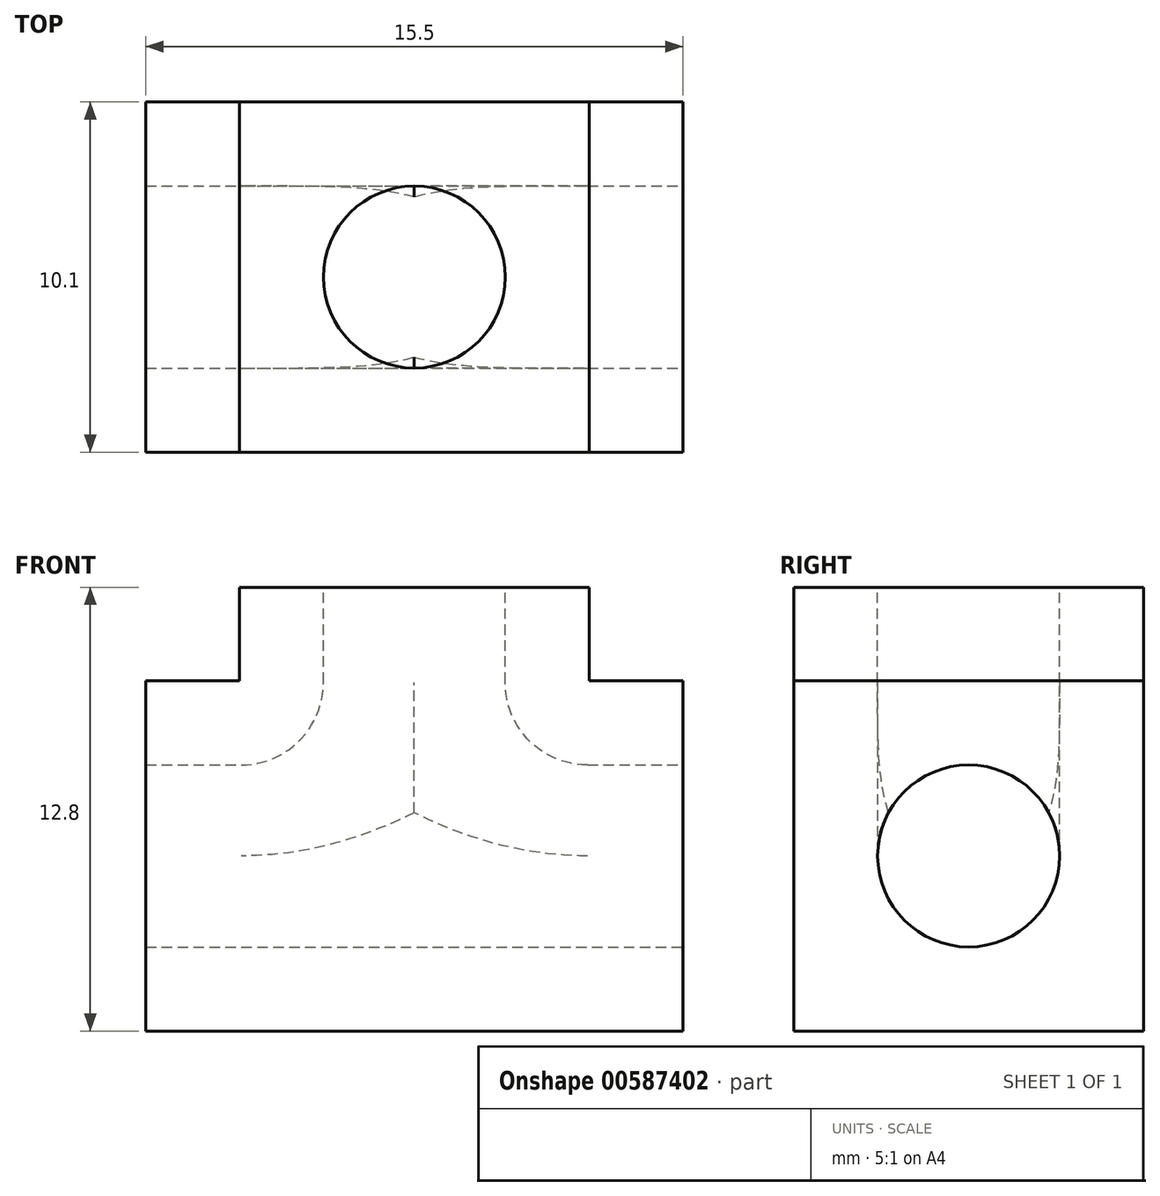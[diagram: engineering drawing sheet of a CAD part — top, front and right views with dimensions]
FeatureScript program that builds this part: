
annotation { "Feature Type Name" : "Feature", "Feature Type Description" : "" }
export const myFeature = defineFeature(function(context is Context, id is Id, definition is map)
    precondition{}
    {
        {
            var Q0;
            Q0=qCreatedBy(makeId("Front.planeOp"),FACE);
            var sketch = newSketch(context, id + "F0", { "sketchPlane" : qUnion([Q0])});
            skLineSegment(sketch, "E0", {"start": v(-15.52, 0) * mm, "end": v(18.58, 0) * mm, "construction": true});
            skLineSegment(sketch, "E1", {"start": v(0, 9.32) * mm, "end": v(0, -7.34) * mm, "construction": true});
            skLineSegment(sketch, "E2", {"start": v(-7.75, -2.75) * mm, "end": v(7.75, -2.75) * mm, "construction": true});
            skLineSegment(sketch, "E3", {"start": v(-2.75, 7.75) * mm, "end": v(-2.75, 2.75) * mm, "construction": true});
            skLineSegment(sketch, "E4.MirrorCS", {"start": v(2.75, 7.75) * mm, "end": v(2.75, 2.75) * mm, "construction": true});
            skLineSegment(sketch, "E5.MirrorCS", {"start": v(-7.75, 2.75) * mm, "end": v(-2.75, 2.75) * mm, "construction": true});
            skLineSegment(sketch, "E6.trimOffspring", {"start": v(2.75, 2.75) * mm, "end": v(7.75, 2.75) * mm, "construction": true});
            skLineSegment(sketch, "E7", {"start": v(-5.05, 7.75) * mm, "end": v(-5.05, 5.05) * mm});
            skLineSegment(sketch, "E8", {"start": v(-7.75, 5.05) * mm, "end": v(-5.05, 5.05) * mm});
            skLineSegment(sketch, "E9", {"start": v(-7.75, -5.05) * mm, "end": v(7.75, -5.05) * mm});
            skLineSegment(sketch, "E10", {"start": v(-5.5, 5.05) * mm, "end": v(-5.5, 2.75) * mm, "construction": true});
            skLineSegment(sketch, "E11", {"start": v(-5.05, 5.69) * mm, "end": v(-2.75, 5.69) * mm, "construction": true});
            skLineSegment(sketch, "E12", {"start": v(2.43, -2.75) * mm, "end": v(2.43, -5.05) * mm, "construction": true});
            skLineSegment(sketch, "E13", {"start": v(-2.75, 5.69) * mm, "end": v(0, 5.69) * mm, "construction": true});
            skLineSegment(sketch, "E14", {"start": v(2.43, -2.75) * mm, "end": v(2.43, 0) * mm, "construction": true});
            skLineSegment(sketch, "E15", {"start": v(-7.75, 2.75) * mm, "end": v(-7.75, -2.75) * mm, "construction": true});
            skLineSegment(sketch, "E16", {"start": v(7.75, 2.75) * mm, "end": v(7.75, -2.75) * mm, "construction": true});
            skLineSegment(sketch, "E17", {"start": v(-2.75, 7.75) * mm, "end": v(2.75, 7.75) * mm, "construction": true});
            skLineSegment(sketch, "E18", {"start": v(-7.75, 0) * mm, "end": v(-7.75, 5.05) * mm});
            skLineSegment(sketch, "E19.MirrorCS", {"start": v(-7.75, 0) * mm, "end": v(-7.75, -5.05) * mm});
            skLineSegment(sketch, "E20", {"start": v(0, 7.75) * mm, "end": v(-5.05, 7.75) * mm});
            skLineSegment(sketch, "E21.MirrorCS", {"start": v(0, 7.75) * mm, "end": v(5.05, 7.75) * mm});
            skLineSegment(sketch, "E22", {"start": v(7.75, 0) * mm, "end": v(7.75, 5.05) * mm});
            skLineSegment(sketch, "E23.MirrorCS", {"start": v(7.75, 0) * mm, "end": v(7.75, -5.05) * mm});
            skLineSegment(sketch, "E24.MirrorCS", {"start": v(5.05, 7.75) * mm, "end": v(5.05, 5.05) * mm});
            skLineSegment(sketch, "E25.MirrorCS", {"start": v(7.75, 5.05) * mm, "end": v(5.05, 5.05) * mm});
            skSolve(sketch);
        }
        {
            var Q0;
            Q0 = qSketchRegion(id + "F0", true);
            extrude(context, id + "F1", {"entities" : qUnion([Q0]), "endBound" : BoundingType.SYMMETRIC, "depth" : 10.1 * mm, "offsetDistance" : 25 * mm});
        }
        {
            var Q0;
            Q0=qCreatedBy(makeId("Right.planeOp"),FACE);
            var sketch = newSketch(context, id + "F2", { "sketchPlane" : qUnion([Q0])});
            skCircle(sketch, "E26", {"center": v(0, 0) * mm, "radius": 2.62 * mm});
            skSolve(sketch);
        }
        {
            var Q0;
            Q0=qCreatedBy(makeId("Front.planeOp"),FACE);
            var sketch = newSketch(context, id + "F3", { "sketchPlane" : qUnion([Q0])});
            skLineSegment(sketch, "E27", {"start": v(11.51, 0) * mm, "end": v(5, 0) * mm});
            skLineSegment(sketch, "E28", {"start": v(-5, 0) * mm, "end": v(-10.6, 0) * mm});
            skPoint(sketch, "E29.visualSharp", {"position": v(0, 0) * mm});
            skLineSegment(sketch, "E30", {"start": v(-10.6, 0) * mm, "end": v(11.51, 0) * mm});
            skSolve(sketch);
        }
        {
            var Q0;
            Q0 = qSketchRegion(id + "F2", true);
            var Q1;
            Q1=sQuery(id+"F3.wireOp",EDGE,"E30");
            sweep(context, id + "F4", {"operationType" : NewBodyOperationType.REMOVE, "profiles" : qUnion([Q0]), "path" : qUnion([Q1])});
        }
        {
            var Q0;
            Q0=makeQuery(id+"F1.opExtrude","SWEPT_FACE",FACE,{"disambiguationData":[OSD([sQuery(id+"F0.wireOp",EDGE,"E20"),sQuery(id+"F0.wireOp",EDGE,"E21.MirrorCS")])]});
            var sketch = newSketch(context, id + "F5", { "sketchPlane" : qUnion([Q0])});
            skCircle(sketch, "E31", {"center": v(0, 0) * mm, "radius": 2.62 * mm});
            skSolve(sketch);
        }
        {
            var Q0;
            Q0=qCreatedBy(makeId("Front.planeOp"),FACE);
            var sketch = newSketch(context, id + "F6", { "sketchPlane" : qUnion([Q0])});
            skLineSegment(sketch, "E32", {"start": v(0, 10.95) * mm, "end": v(0, 5) * mm});
            skLineSegment(sketch, "E33", {"start": v(-5, 0) * mm, "end": v(-12.53, 0) * mm});
            skPoint(sketch, "E34.visualSharp", {"position": v(0, 0) * mm});
            skArc(sketch, "E34.filletArc", {"start": v(-5, 0) * mm, "mid": v(-1.46, 1.46) * mm, "end": v(0, 5) * mm});
            skLineSegment(sketch, "E35", {"start": v(5, 0) * mm, "end": v(12.61, 0) * mm});
            skArc(sketch, "E36.filletArc", {"start": v(0, 5) * mm, "mid": v(1.46, 1.46) * mm, "end": v(5, 0) * mm});
            skSolve(sketch);
        }
        {
            var Q0;
            Q0 = qSketchRegion(id + "F5", true);
            var Q1;
            Q1=sQuery(id+"F6.wireOp",EDGE,"E32");
            var Q2;
            Q2=sQuery(id+"F6.wireOp",EDGE,"E36.filletArc");
            sweep(context, id + "F7", {"operationType" : NewBodyOperationType.REMOVE, "profiles" : qUnion([Q0]), "path" : qUnion([Q1, Q2])});
        }
        {
            var Q0;
            Q0 = qSketchRegion(id + "F5", true);
            var Q1;
            Q1=sQuery(id+"F6.wireOp",EDGE,"E32");
            var Q2;
            Q2=sQuery(id+"F6.wireOp",EDGE,"E34.filletArc");
            sweep(context, id + "F8", {"operationType" : NewBodyOperationType.REMOVE, "profiles" : qUnion([Q0]), "path" : qUnion([Q1, Q2])});
        }
    });
